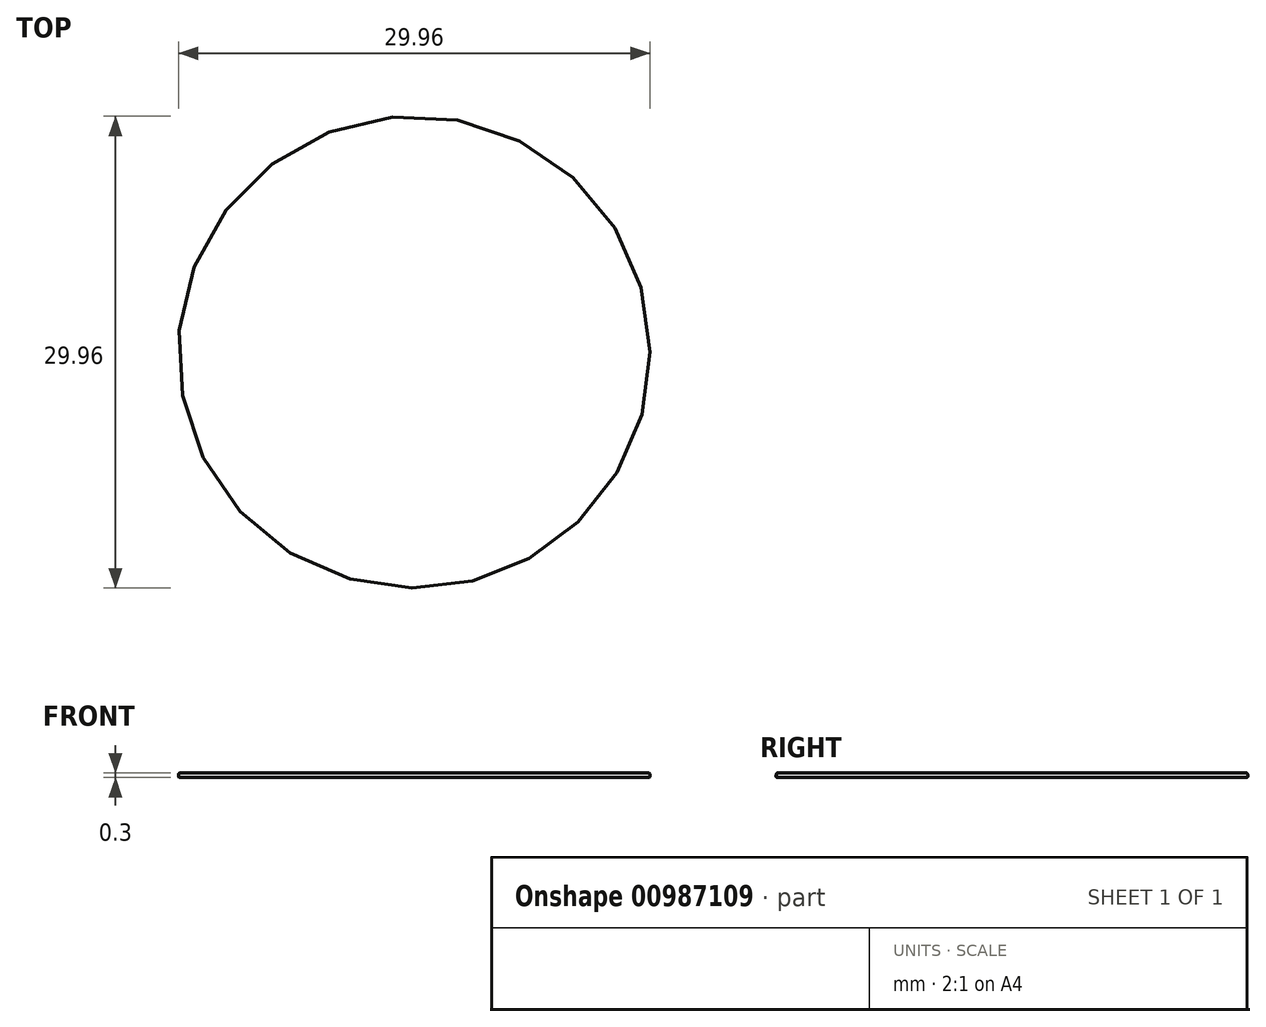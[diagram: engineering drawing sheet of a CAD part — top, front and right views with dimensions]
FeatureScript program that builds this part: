
annotation { "Feature Type Name" : "Feature", "Feature Type Description" : "" }
export const myFeature = defineFeature(function(context is Context, id is Id, definition is map)
    precondition{}
    {
        {
            var Q0;
            Q0=qCreatedBy(makeId("Top.planeOp"),FACE);
            var sketch = newSketch(context, id + "F0", { "sketchPlane" : qUnion([Q0])});
            skCircle(sketch, "E0", {"center": v(0, 0) * mm, "radius": 15 * mm});
            skSolve(sketch);
        }
        {
            var Q0;
            Q0 = qSketchRegion(id + "F0", true);
            extrude(context, id + "F1", {"entities" : qUnion([Q0]), "depth" : 0.3 * mm, "offsetDistance" : 25 * mm, "hasDraft" : true, "draftAngle" : 8 * degree, "draftPullDirection" : true});
        }
        {
            var Q0;
            Q0=makeQuery(id+"F1.opExtrude","CAP_EDGE",EDGE,{"disambiguationData":[OSD([sQuery(id+"F0.wireOp",EDGE,"E0")])],"isStart":false});
            var Q1;
            Q1=makeQuery(id+"F1.opExtrude","CAP_EDGE",EDGE,{"disambiguationData":[OSD([sQuery(id+"F0.wireOp",EDGE,"E0")])],"isStart":true});
            fillet(context, id + "F2", {"entities" : qUnion([Q0, Q1]), "radius" : 0.1 * mm, "tangentPropagation" : true, "allowEdgeOverflow" : false});
        }
    });
